# Revit family: QF_MOFFAT WALDORF_BPL8120E
name_source: partatom
category: Specialty Equipment
revit_build: Autodesk Revit Architecture 2012 (Build: 20110916_2132(x64)
units: mm (PartAtom-declared; Revit-internal decimal feet)

## types (1)
- QF_MOFFAT WALDORF_BPL8120E
    Apparent Power = 16513 VA
    Body Finish = QF_Finishes_Stainless Steel
    Cold Water Connection Height = 0 mm  [stored 0 ft]
    Cold Water Flow = 0 GPM
    Cold Water Maximum Pressure = 0.00 psi
    Cold Water Minimum Pressure = 0.00 psi
    Cold Water Size = 1"
    Cold Water Temperature Recommended = -460 °F
    Conn Conduit = Yes
    Cycle = 50 Hz
    Depth = 805 mm  [stored 2.64108 ft]
    Description = BRATT PAN LOW SPLASHBACK 120 L ELECTRIC WITH MANUAL LIFT
    Elec Conn Connection Height = 0 mm  [stored 0 ft]
    Elec Conn RI Height = 0 mm  [stored 0 ft]
    FL Amps = 23 A
    Height = 970 mm  [stored 3.18241 ft]
    Manufacturer = MOFFAT WALDORF
    Max Overcurrent Protection = 0 A
    Min Ckt Ampacity = 0 A
    Model = BPL8120E
    Number of Poles = 1
    Phase = 3
    URL = www.moffat.com
    URL Cutsheet = www.moffat.com
    Volts = 415 V
    Watts = 17000 W
    Weight in Pounds = 485.0164
    Width = 1200 mm

note: [stored X ft] marks values corroborated as IEEE doubles in the binary element streams (Revit-internal decimal feet)

## geometry (parser evidence)
native form markers: Blend x6, Sweep x6
no freeform markers — native parametric forms only
